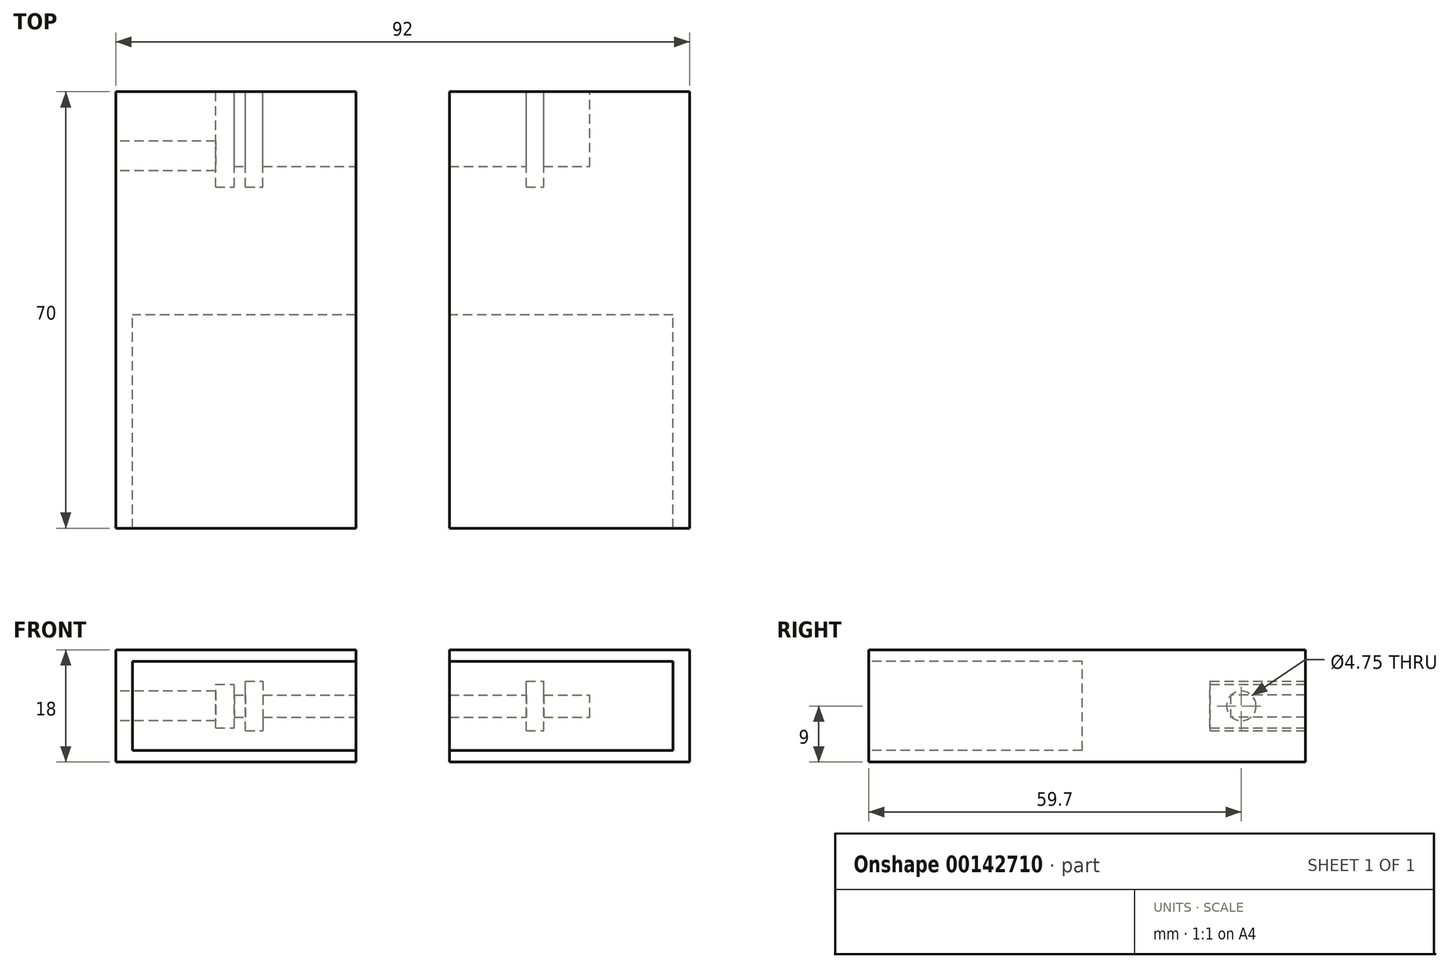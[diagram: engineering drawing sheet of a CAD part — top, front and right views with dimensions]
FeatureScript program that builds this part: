
annotation { "Feature Type Name" : "Feature", "Feature Type Description" : "" }
export const myFeature = defineFeature(function(context is Context, id is Id, definition is map)
    precondition{}
    {
        {
            var Q0;
            Q0=qCreatedBy(makeId("Front.planeOp"),FACE);
            var sketch = newSketch(context, id + "F0", { "sketchPlane" : qUnion([Q0])});
            skLineSegment(sketch, "E0.bottom", {"start": v(46, -9) * mm, "end": v(-46, -9) * mm});
            skLineSegment(sketch, "E0.top", {"start": v(46, 9) * mm, "end": v(-46, 9) * mm});
            skLineSegment(sketch, "E0.left", {"start": v(46, -9) * mm, "end": v(46, 9) * mm});
            skLineSegment(sketch, "E0.right", {"start": v(-46, -9) * mm, "end": v(-46, 9) * mm});
            skPoint(sketch, "E0.middle", {"position": v(0, 0) * mm});
            skLineSegment(sketch, "E1.bottom", {"start": v(43.33, -7.12) * mm, "end": v(-43.33, -7.13) * mm});
            skLineSegment(sketch, "E1.top", {"start": v(43.33, 7.13) * mm, "end": v(-43.33, 7.12) * mm});
            skLineSegment(sketch, "E1.left", {"start": v(43.33, -7.12) * mm, "end": v(43.33, 7.13) * mm});
            skLineSegment(sketch, "E1.right", {"start": v(-43.33, -7.13) * mm, "end": v(-43.33, 7.12) * mm});
            skSolve(sketch);
        }
        {
            var Q0;
            Q0=makeQuery(id+"F0.imprint","IMPRINT",FACE,{"disambiguationData":[TD([[makeQuery(id+"F0.imprint","IMPRINT",EDGE,{"derivedFrom":sQuery(id+"F0.wireOp",EDGE,"E0.bottom")}),-1.0]])]});
            extrude(context, id + "F1", {"entities" : qUnion([Q0]), "depth" : 70 * mm, "offsetDistance" : 25 * mm});
        }
        {
            var Q0;
            Q0=makeQuery(id+"F0.imprint","IMPRINT",FACE,{"disambiguationData":[TD([[makeQuery(id+"F0.imprint","IMPRINT",EDGE,{"derivedFrom":sQuery(id+"F0.wireOp",EDGE,"E1.bottom")}),-1.0]])]});
            extrude(context, id + "F2", {"entities" : qUnion([Q0]), "operationType" : NewBodyOperationType.ADD, "depth" : 35.8 * mm, "offsetDistance" : 25 * mm});
        }
        {
            var Q0;
            Q0=qCreatedBy(makeId("Front.planeOp"),FACE);
            var sketch = newSketch(context, id + "F3", { "sketchPlane" : qUnion([Q0])});
            skPoint(sketch, "E2.middle", {"position": v(0, 0) * mm});
            skCircle(sketch, "E3", {"center": v(0, 0) * mm, "radius": 2 * mm});
            skSolve(sketch);
        }
        {
            var Q0;
            Q0=makeQuery(id+"F2.opExtrude","CAP_FACE",FACE,{"disambiguationData":[OSD([sQuery(id+"F0.wireOp",EDGE,"E1.bottom"),sQuery(id+"F0.wireOp",EDGE,"E1.top"),sQuery(id+"F0.wireOp",EDGE,"E1.left"),sQuery(id+"F0.wireOp",EDGE,"E1.right")])],"isStart":false});
            var sketch = newSketch(context, id + "F4", { "sketchPlane" : qUnion([Q0])});
            skLineSegment(sketch, "E4.bottom", {"start": v(6.65, -4.3) * mm, "end": v(-6.65, -4.3) * mm});
            skLineSegment(sketch, "E4.top", {"start": v(6.65, 4.3) * mm, "end": v(-6.65, 4.3) * mm});
            skLineSegment(sketch, "E4.left", {"start": v(6.65, -4.3) * mm, "end": v(6.65, 4.3) * mm});
            skLineSegment(sketch, "E4.right", {"start": v(-6.65, -4.3) * mm, "end": v(-6.65, 4.3) * mm});
            skPoint(sketch, "E4.middle", {"position": v(0, 0) * mm});
            skSolve(sketch);
        }
        {
            var Q0;
            Q0=makeQuery(id+"F4.imprint","IMPRINT",FACE,{"disambiguationData":[TD([[makeQuery(id+"F4.imprint","IMPRINT",EDGE,{"derivedFrom":sQuery(id+"F4.wireOp",EDGE,"E4.bottom")}),-1.0]])]});
            extrude(context, id + "F5", {"entities" : qUnion([Q0]), "operationType" : NewBodyOperationType.REMOVE, "oppositeDirection" : true, "depth" : 22 * mm, "offsetDistance" : 25 * mm});
        }
        {
            var Q0;
            Q0=qSketchRegion(id+"F3",true);
            extrude(context, id + "F6", {"entities" : qUnion([Q0]), "operationType" : NewBodyOperationType.REMOVE, "depth" : 8 * mm, "offsetDistance" : 25 * mm});
        }
        {
            var Q0;
            Q0=qCreatedBy(makeId("Front.planeOp"),FACE);
            var sketch = newSketch(context, id + "F7", { "sketchPlane" : qUnion([Q0])});
            skLineSegment(sketch, "E5.bottom", {"start": v(-13.25, -2) * mm, "end": v(13.25, -2) * mm});
            skLineSegment(sketch, "E5.top", {"start": v(-17.25, 2) * mm, "end": v(17.25, 2) * mm});
            skLineSegment(sketch, "E5.left", {"start": v(-20, -2) * mm, "end": v(-20, -0.75) * mm});
            skLineSegment(sketch, "E5.right", {"start": v(20, -2) * mm, "end": v(20, -0.75) * mm});
            skPoint(sketch, "E5.middle", {"position": v(0, 0) * mm});
            skLineSegment(sketch, "E6.bottom", {"start": v(17.25, 2) * mm, "end": v(16, 2) * mm});
            skLineSegment(sketch, "E6.top", {"start": v(20, -9.8) * mm, "end": v(16, -9.8) * mm});
            skLineSegment(sketch, "E6.left", {"start": v(20, -0.75) * mm, "end": v(20, -9.8) * mm});
            skLineSegment(sketch, "E6.right", {"start": v(16, -4.75) * mm, "end": v(16, -9.8) * mm});
            skLineSegment(sketch, "E7.bottom", {"start": v(-17.25, 2) * mm, "end": v(-16, 2) * mm});
            skLineSegment(sketch, "E7.top", {"start": v(-20, -11.9) * mm, "end": v(-16, -11.9) * mm});
            skLineSegment(sketch, "E7.left", {"start": v(-20, -0.75) * mm, "end": v(-20, -11.9) * mm});
            skLineSegment(sketch, "E7.right", {"start": v(-16, -4.75) * mm, "end": v(-16, -11.9) * mm});
            skPoint(sketch, "E8.visualSharp", {"position": v(-16, -2) * mm});
            skArc(sketch, "E8.filletArc", {"start": v(-13.25, -2) * mm, "mid": v(-15.2, -2.8) * mm, "end": v(-16, -4.75) * mm});
            skPoint(sketch, "E9.visualSharp", {"position": v(16, -2) * mm});
            skArc(sketch, "E9.filletArc", {"start": v(16, -4.75) * mm, "mid": v(15.2, -2.8) * mm, "end": v(13.25, -2) * mm});
            skPoint(sketch, "E10.visualSharp", {"position": v(-20, 2) * mm});
            skArc(sketch, "E10.filletArc", {"start": v(-17.25, 2) * mm, "mid": v(-19.2, 1.2) * mm, "end": v(-20, -0.75) * mm});
            skPoint(sketch, "E11.visualSharp", {"position": v(20, 2) * mm});
            skArc(sketch, "E11.filletArc", {"start": v(20, -0.75) * mm, "mid": v(19.2, 1.2) * mm, "end": v(17.25, 2) * mm});
            skSolve(sketch);
        }
        {
            var Q0;
            Q0=makeQuery(id+"F5.boolean.opBoolean","COPY",FACE,{"derivedFrom":makeQuery(id+"F5.opExtrude","CAP_FACE",FACE,{"disambiguationData":[OSD([sQuery(id+"F4.wireOp",EDGE,"E4.bottom"),sQuery(id+"F4.wireOp",EDGE,"E4.top"),sQuery(id+"F4.wireOp",EDGE,"E4.left"),sQuery(id+"F4.wireOp",EDGE,"E4.right")])],"isStart":false})});
            var sketch = newSketch(context, id + "F8", { "sketchPlane" : qUnion([Q0])});
            skCircle(sketch, "E12", {"center": v(0, -0.7) * mm, "radius": 3.2 * mm});
            skLineSegment(sketch, "E13.bottom", {"start": v(5.4, -3.92) * mm, "end": v(-5.4, -3.92) * mm});
            skLineSegment(sketch, "E13.top", {"start": v(5.4, 2.53) * mm, "end": v(-5.4, 2.53) * mm});
            skLineSegment(sketch, "E13.left", {"start": v(5.4, -3.92) * mm, "end": v(5.4, 2.53) * mm});
            skLineSegment(sketch, "E13.right", {"start": v(-5.4, -3.92) * mm, "end": v(-5.4, 2.53) * mm});
            skSolve(sketch);
        }
        {
            var Q0;
            Q0=makeQuery(id+"F8.imprint","IMPRINT",FACE,{"disambiguationData":[TD([[makeQuery(id+"F8.imprint","IMPRINT",EDGE,{"derivedFrom":sQuery(id+"F8.wireOp",EDGE,"E12")}),1.0]])]});
            var Q1;
            Q1=makeQuery(id+"F8.imprint","IMPRINT",FACE,{"disambiguationData":[TD([[makeQuery(id+"F8.imprint","IMPRINT",EDGE,{"derivedFrom":sQuery(id+"F8.wireOp",EDGE,"E12")}),-1.0]])]});
            extrude(context, id + "F9", {"entities" : qUnion([Q0, Q1]), "operationType" : NewBodyOperationType.REMOVE, "oppositeDirection" : true, "depth" : 9.9 * mm, "offsetDistance" : 25 * mm});
        }
        {
            var Q0;
            Q0=makeQuery(id+"F1.opExtrude","SWEPT_FACE",FACE,{"disambiguationData":[OSD([sQuery(id+"F0.wireOp",EDGE,"E0.bottom")])]});
            var sketch = newSketch(context, id + "F10", { "sketchPlane" : qUnion([Q0])});
            skPoint(sketch, "E14", {"position": v(0, 1.31) * mm});
            skLineSegment(sketch, "E15.bottom", {"start": v(7.5, -78.69) * mm, "end": v(-7.5, -78.69) * mm});
            skLineSegment(sketch, "E15.top", {"start": v(7.5, 81.31) * mm, "end": v(-7.5, 81.31) * mm});
            skLineSegment(sketch, "E15.left", {"start": v(7.5, -78.69) * mm, "end": v(7.5, 81.31) * mm});
            skLineSegment(sketch, "E15.right", {"start": v(-7.5, -78.69) * mm, "end": v(-7.5, 81.31) * mm});
            skSolve(sketch);
        }
        {
            var Q0;
            {var subQ0=sQuery(id+"F10.wireOp",EDGE,"E15.left");var subQ5=sQuery(id+"F0.wireOp",EDGE,"E0.bottom");var subQ8=makeQuery(id+"F1.opExtrude","CAP_EDGE",EDGE,{"disambiguationData":[OSD([subQ5])],"isStart":false});var subQ9=makeQuery(id+"F10.imprint","INTERSECT",VERTEX,{"derivedFrom":[subQ8,subQ0]});Q0=makeQuery(id+"F10.imprint","IMPRINT",FACE,{"disambiguationData":[TD([[makeQuery(id+"F10.imprint","IMPRINT",EDGE,{"disambiguationData":[TD([[subQ9,-1.0]])],"derivedFrom":subQ8}),1.0]])]});}
            extrude(context, id + "F11", {"entities" : qUnion([Q0]), "operationType" : NewBodyOperationType.REMOVE, "oppositeDirection" : true, "depth" : 24.4 * mm, "offsetDistance" : 25 * mm});
        }
        {
            var Q0;
            Q0=makeQuery(id+"F2.opExtrude","CAP_FACE",FACE,{"disambiguationData":[OSD([sQuery(id+"F0.wireOp",EDGE,"E1.bottom"),sQuery(id+"F0.wireOp",EDGE,"E1.top"),sQuery(id+"F0.wireOp",EDGE,"E1.left"),sQuery(id+"F0.wireOp",EDGE,"E1.right")])],"isStart":false});
            var sketch = newSketch(context, id + "F12", { "sketchPlane" : qUnion([Q0])});
            skPoint(sketch, "E16", {"position": v(-24.97, 0) * mm});
            skPoint(sketch, "E17", {"position": v(24.97, 0) * mm});
            skCircle(sketch, "E18", {"center": v(-24.97, 0) * mm, "radius": 4.9 * mm});
            skCircle(sketch, "E19", {"center": v(24.97, 0) * mm, "radius": 4.9 * mm});
            skCircle(sketch, "E20", {"center": v(-24.97, 0) * mm, "radius": 2.12 * mm});
            skCircle(sketch, "E21", {"center": v(24.97, 0) * mm, "radius": 2.12 * mm});
            skPoint(sketch, "E22.orphan", {"position": v(-43.33, 0) * mm});
            skPoint(sketch, "E23.end.orphan", {"position": v(-6.62, 0) * mm});
            skPoint(sketch, "E24.orphan", {"position": v(6.62, 0) * mm});
            skPoint(sketch, "E25.end.orphan", {"position": v(43.33, 0) * mm});
            skSolve(sketch);
        }
        {
            var Q0;
            Q0=makeQuery(id+"F0.imprint","IMPRINT",FACE,{"disambiguationData":[TD([[makeQuery(id+"F0.imprint","IMPRINT",EDGE,{"derivedFrom":sQuery(id+"F0.wireOp",EDGE,"E1.bottom")}),-1.0]])]});
            var sketch = newSketch(context, id + "F13", { "sketchPlane" : qUnion([Q0])});
            skLineSegment(sketch, "E26.bottom", {"start": v(-27, -1.77) * mm, "end": v(-25.21, -1.77) * mm});
            skLineSegment(sketch, "E26.top", {"start": v(-27, 1.77) * mm, "end": v(-25.21, 1.77) * mm});
            skLineSegment(sketch, "E26.left", {"start": v(-30, -1.77) * mm, "end": v(-30, 1.78) * mm});
            skLineSegment(sketch, "E26.right", {"start": v(30, -1.78) * mm, "end": v(30, 1.77) * mm});
            skPoint(sketch, "E26.middle", {"position": v(0, 0) * mm});
            skPoint(sketch, "E27", {"position": v(-28.5, 0) * mm});
            skLineSegment(sketch, "E28.bottom", {"start": v(-30, -3.5) * mm, "end": v(-27, -3.5) * mm});
            skLineSegment(sketch, "E28.top", {"start": v(-30, 3.5) * mm, "end": v(-27, 3.5) * mm});
            skLineSegment(sketch, "E28.left", {"start": v(-30, -3.5) * mm, "end": v(-30, 3.5) * mm});
            skLineSegment(sketch, "E28.right", {"start": v(-27, -3.5) * mm, "end": v(-27, -1.77) * mm});
            skPoint(sketch, "E29.orphan", {"position": v(-27, 0) * mm});
            skPoint(sketch, "E30.end.orphan", {"position": v(-30, 0) * mm});
            skLineSegment(sketch, "E31.trimOffspring", {"start": v(-27, 1.78) * mm, "end": v(-27, 3.5) * mm});
            skLineSegment(sketch, "E32.bottom", {"start": v(-25.21, -3.99) * mm, "end": v(-22.41, -3.99) * mm});
            skLineSegment(sketch, "E32.top", {"start": v(-25.21, 4) * mm, "end": v(-22.41, 4) * mm});
            skLineSegment(sketch, "E32.left", {"start": v(-25.21, -3.99) * mm, "end": v(-25.21, -1.77) * mm});
            skLineSegment(sketch, "E32.right", {"start": v(-22.41, -3.99) * mm, "end": v(-22.41, -1.77) * mm});
            skPoint(sketch, "E32.middle", {"position": v(-23.81, 0) * mm});
            skLineSegment(sketch, "E33.trimOffspring", {"start": v(-22.41, 1.77) * mm, "end": v(19.79, 1.77) * mm});
            skLineSegment(sketch, "E34.trimOffspring", {"start": v(-22.41, 1.77) * mm, "end": v(-22.41, 4) * mm});
            skLineSegment(sketch, "E35.trimOffspring", {"start": v(-25.21, 1.77) * mm, "end": v(-25.21, 4) * mm});
            skLineSegment(sketch, "E36.trimOffspring", {"start": v(-22.41, -1.77) * mm, "end": v(19.79, -1.77) * mm});
            skPoint(sketch, "E37", {"position": v(21.19, 0) * mm});
            skLineSegment(sketch, "E38.bottom", {"start": v(19.79, -3.99) * mm, "end": v(22.59, -3.99) * mm});
            skLineSegment(sketch, "E38.top", {"start": v(19.79, 4) * mm, "end": v(22.59, 4) * mm});
            skLineSegment(sketch, "E38.left", {"start": v(19.79, -3.99) * mm, "end": v(19.79, -1.77) * mm});
            skLineSegment(sketch, "E38.right", {"start": v(22.59, -3.99) * mm, "end": v(22.59, -1.77) * mm});
            skPoint(sketch, "E39.orphan", {"position": v(22.59, 0) * mm});
            skPoint(sketch, "E40.start.orphan", {"position": v(19.79, 0) * mm});
            skPoint(sketch, "E41.orphan", {"position": v(19.79, 1.78) * mm});
            skPoint(sketch, "E42.end.orphan", {"position": v(19.79, -1.77) * mm});
            skLineSegment(sketch, "E43.trimOffspring", {"start": v(19.79, 1.78) * mm, "end": v(19.79, 4) * mm});
            skLineSegment(sketch, "E44.trimOffspring", {"start": v(22.59, 1.77) * mm, "end": v(22.59, 4) * mm});
            skLineSegment(sketch, "E45.trimOffspring", {"start": v(22.59, 1.77) * mm, "end": v(30, 1.77) * mm});
            skLineSegment(sketch, "E46.trimOffspring", {"start": v(22.59, -1.77) * mm, "end": v(30, -1.77) * mm});
            skLineSegment(sketch, "E47", {"start": v(22.59, 1.77) * mm, "end": v(22.59, -1.77) * mm});
            skLineSegment(sketch, "E48", {"start": v(19.79, 1.77) * mm, "end": v(19.79, -1.77) * mm});
            skLineSegment(sketch, "E49", {"start": v(-22.41, 1.77) * mm, "end": v(-22.41, -1.77) * mm});
            skLineSegment(sketch, "E50", {"start": v(-25.21, 1.77) * mm, "end": v(-25.21, -1.77) * mm});
            skLineSegment(sketch, "E51", {"start": v(-27, 1.78) * mm, "end": v(-27, -1.77) * mm});
            skSolve(sketch);
        }
        {
            var Q0;
            Q0=makeQuery(id+"F13.imprint","IMPRINT",FACE,{"disambiguationData":[TD([[makeQuery(id+"F13.imprint","IMPRINT",EDGE,{"derivedFrom":sQuery(id+"F13.wireOp",EDGE,"E26.right")}),1.0]])]});
            var Q1;
            Q1=makeQuery(id+"F13.imprint","IMPRINT",FACE,{"disambiguationData":[TD([[makeQuery(id+"F13.imprint","IMPRINT",EDGE,{"derivedFrom":sQuery(id+"F13.wireOp",EDGE,"E33.trimOffspring")}),-1.0]])]});
            var Q2;
            Q2=makeQuery(id+"F13.imprint","IMPRINT",FACE,{"disambiguationData":[TD([[makeQuery(id+"F13.imprint","IMPRINT",EDGE,{"derivedFrom":sQuery(id+"F13.wireOp",EDGE,"E26.bottom")}),1.0]])]});
            extrude(context, id + "F14", {"entities" : qUnion([Q0, Q1, Q2]), "operationType" : NewBodyOperationType.REMOVE, "depth" : 12 * mm, "offsetDistance" : 25 * mm});
        }
        {
            var Q0;
            Q0=makeQuery(id+"F13.imprint","IMPRINT",FACE,{"disambiguationData":[TD([[makeQuery(id+"F13.imprint","IMPRINT",EDGE,{"derivedFrom":sQuery(id+"F13.wireOp",EDGE,"E38.bottom")}),1.0]])]});
            var Q1;
            Q1=makeQuery(id+"F13.imprint","IMPRINT",FACE,{"disambiguationData":[TD([[makeQuery(id+"F13.imprint","IMPRINT",EDGE,{"derivedFrom":sQuery(id+"F13.wireOp",EDGE,"E32.bottom")}),1.0]])]});
            var Q2;
            {var subQ3=sQuery(id+"F13.wireOp",EDGE,"E28.bottom");Q2=makeQuery(id+"F13.imprint","IMPRINT",FACE,{"disambiguationData":[TD([[makeQuery(id+"F13.imprint","IMPRINT",EDGE,{"derivedFrom":subQ3}),1.0]])]});}
            extrude(context, id + "F15", {"entities" : qUnion([Q0, Q1, Q2]), "operationType" : NewBodyOperationType.REMOVE, "depth" : 15.3 * mm, "offsetDistance" : 25 * mm});
        }
        {
            var Q0;
            Q0=makeQuery(id+"F1.opExtrude","SWEPT_FACE",FACE,{"disambiguationData":[OSD([sQuery(id+"F0.wireOp",EDGE,"E0.right")])]});
            var sketch = newSketch(context, id + "F16", { "sketchPlane" : qUnion([Q0])});
            skLineSegment(sketch, "E52", {"start": v(0, 0) * mm, "end": v(10.3, 0) * mm});
            skCircle(sketch, "E53", {"center": v(10.3, 0) * mm, "radius": 2.38 * mm});
            skSolve(sketch);
        }
        {
            var Q0;
            Q0=makeQuery(id+"F16.imprint","IMPRINT",FACE,{"disambiguationData":[TD([[makeQuery(id+"F16.imprint","IMPRINT",EDGE,{"derivedFrom":sQuery(id+"F16.wireOp",EDGE,"E53")}),1.0]])]});
            extrude(context, id + "F17", {"entities" : qUnion([Q0]), "operationType" : NewBodyOperationType.REMOVE, "oppositeDirection" : true, "depth" : 16.6 * mm, "offsetDistance" : 25 * mm});
        }
    });
